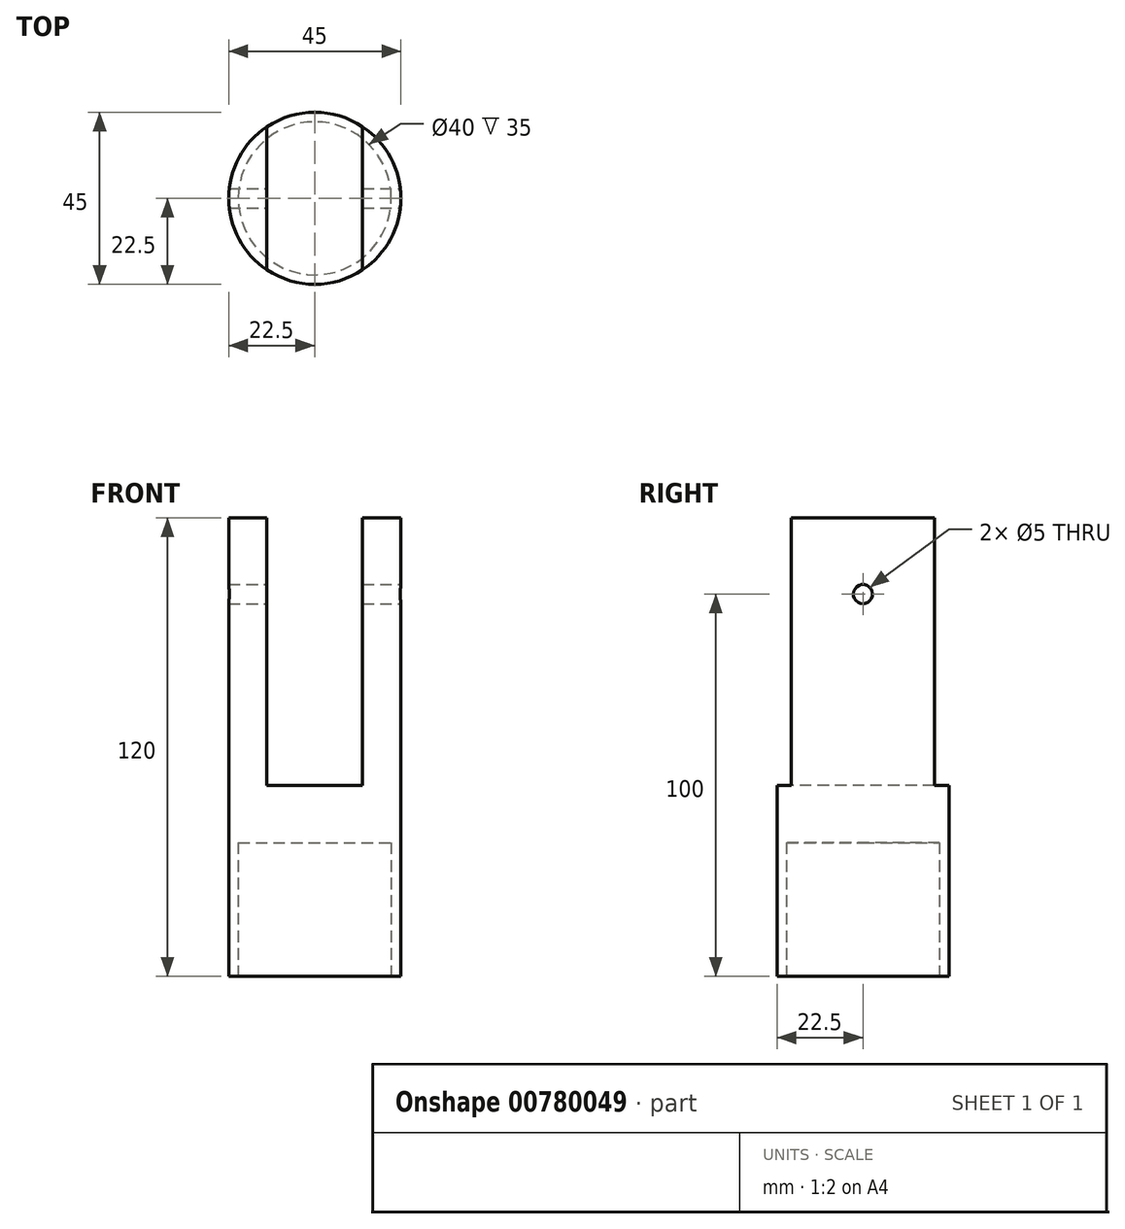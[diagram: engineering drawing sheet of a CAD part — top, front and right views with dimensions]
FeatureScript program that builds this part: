
annotation { "Feature Type Name" : "Feature", "Feature Type Description" : "" }
export const myFeature = defineFeature(function(context is Context, id is Id, definition is map)
    precondition{}
    {
        {
            var Q0;
            Q0=qCreatedBy(makeId("Top.planeOp"),FACE);
            var sketch = newSketch(context, id + "F0", { "sketchPlane" : qUnion([Q0])});
            skCircle(sketch, "E0", {"center": v(0, 0) * mm, "radius": 22.5 * mm});
            skSolve(sketch);
        }
        {
            var Q0;
            Q0=makeQuery(id+"F0.imprint","IMPRINT",FACE,{"disambiguationData":[TD([[makeQuery(id+"F0.imprint","IMPRINT",EDGE,{"derivedFrom":sQuery(id+"F0.wireOp",EDGE,"E0")}),1.0]])]});
            extrude(context, id + "F1", {"entities" : qUnion([Q0]), "depth" : 120 * mm, "offsetDistance" : 25 * mm});
        }
        {
            var Q0;
            Q0=makeQuery(id+"F1.opExtrude","CAP_FACE",FACE,{"disambiguationData":[OSD([sQuery(id+"F0.wireOp",EDGE,"E0")])],"isStart":false});
            var sketch = newSketch(context, id + "F2", { "sketchPlane" : qUnion([Q0])});
            skLineSegment(sketch, "E1", {"start": v(-12.5, 18.7) * mm, "end": v(-12.5, -18.7) * mm});
            skLineSegment(sketch, "E2", {"start": v(12.5, 18.7) * mm, "end": v(12.5, -18.7) * mm});
            skSolve(sketch);
        }
        {
            var Q0;
            Q0=makeQuery(id+"F1.opExtrude","CAP_FACE",FACE,{"disambiguationData":[OSD([sQuery(id+"F0.wireOp",EDGE,"E0")])],"isStart":false});
            var sketch = newSketch(context, id + "F3", { "sketchPlane" : qUnion([Q0])});
            skLineSegment(sketch, "E3", {"start": v(-12.5, 18.7) * mm, "end": v(-12.5, -18.7) * mm});
            skLineSegment(sketch, "E4", {"start": v(12.5, 18.7) * mm, "end": v(12.5, -18.7) * mm});
            skSolve(sketch);
        }
        {
            var Q0;
            {var subQ0=sQuery(id+"F2.wireOp",EDGE,"E1");Q0=makeQuery(id+"F2.imprint","IMPRINT",FACE,{"disambiguationData":[TD([[makeQuery(id+"F2.imprint","IMPRINT",EDGE,{"derivedFrom":subQ0}),1.0]])]});}
            extrude(context, id + "F4", {"entities" : qUnion([Q0]), "operationType" : NewBodyOperationType.REMOVE, "oppositeDirection" : true, "depth" : 70 * mm, "offsetDistance" : 25 * mm});
        }
        {
            var Q0;
            Q0=makeQuery(id+"F1.opExtrude","CAP_FACE",FACE,{"disambiguationData":[OSD([sQuery(id+"F0.wireOp",EDGE,"E0")])],"isStart":true});
            var sketch = newSketch(context, id + "F5", { "sketchPlane" : qUnion([Q0])});
            skCircle(sketch, "E5", {"center": v(0, 0) * mm, "radius": 20 * mm});
            skSolve(sketch);
        }
        {
            var Q0;
            Q0=makeQuery(id+"F5.imprint","IMPRINT",FACE,{"disambiguationData":[TD([[makeQuery(id+"F5.imprint","IMPRINT",EDGE,{"derivedFrom":sQuery(id+"F5.wireOp",EDGE,"E5")}),1.0]])]});
            extrude(context, id + "F6", {"entities" : qUnion([Q0]), "operationType" : NewBodyOperationType.REMOVE, "oppositeDirection" : true, "depth" : 35 * mm, "offsetDistance" : 25 * mm});
        }
        {
            var Q0;
            Q0=qCreatedBy(makeId("Right.planeOp"),FACE);
            cPlane(context, id + "F7", {"entities" : qUnion([Q0]), "cplaneType" : CPlaneType.OFFSET, "offset" : 22.5 * mm, "width" : 150 * mm, "height" : 150 * mm});
        }
        {
            var Q0;
            Q0=qCreatedBy(id+"F7.planeOp",FACE);
            var sketch = newSketch(context, id + "F8", { "sketchPlane" : qUnion([Q0])});
            skLineSegment(sketch, "E6", {"start": v(-18.7, 100) * mm, "end": v(18.7, 100) * mm});
            skPoint(sketch, "E7", {"position": v(0, 100) * mm});
            skSolve(sketch);
        }
        {
            var Q0;
            Q0=sQuery(id+"F8.wireOp",VERTEX,"E7");
            var Q1;
            Q1=makeQuery(id+"F1.opExtrude","SWEPT_BODY",BODY,{"disambiguationData":[OSD([sQuery(id+"F0.wireOp",EDGE,"E0")])]});
            hole(context, id + "F9", {"style" : HoleStyle.SIMPLE, "endStyle" : HoleEndStyle.THROUGH, "holeDiameter" : 5 * mm, "majorDiameter" : 5 * mm, "isTappedThrough" : true, "tappedDepth" : 12 * mm, "tapClearance" : 3, "locations" : qUnion([Q0]), "scope" : qUnion([Q1])});
        }
    });
